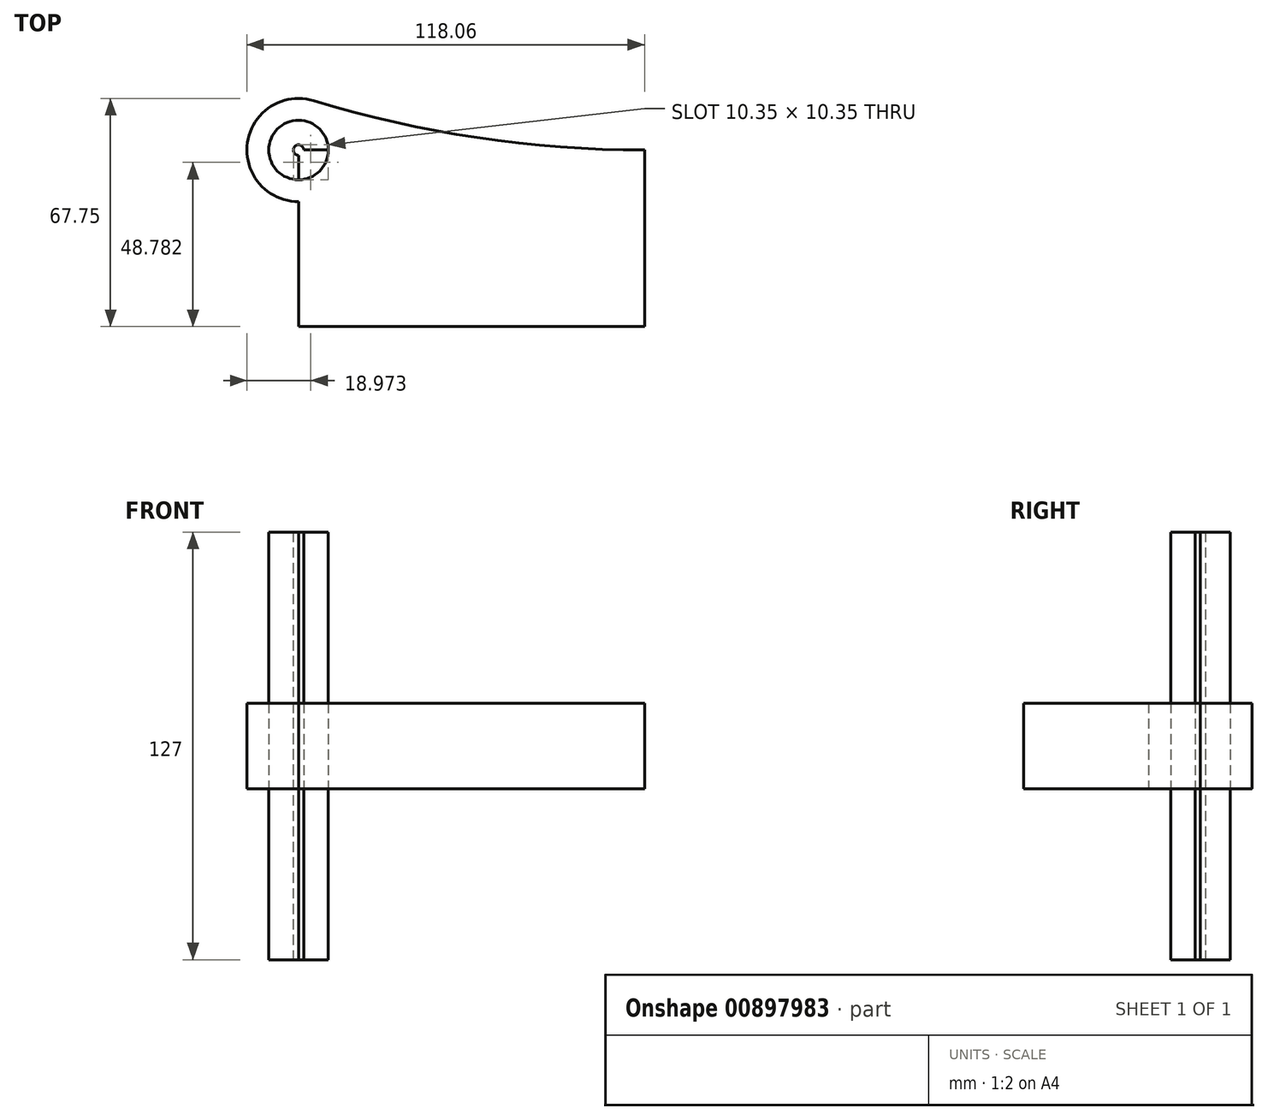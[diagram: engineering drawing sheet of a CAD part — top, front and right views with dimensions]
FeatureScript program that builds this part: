
annotation { "Feature Type Name" : "Feature", "Feature Type Description" : "" }
export const myFeature = defineFeature(function(context is Context, id is Id, definition is map)
    precondition{}
    {
        {
            var Q0;
            Q0=qCreatedBy(makeId("Top.planeOp"),FACE);
            var sketch = newSketch(context, id + "F0", { "sketchPlane" : qUnion([Q0])});
            skLineSegment(sketch, "E0.bottom", {"start": v(51.37, -26.22) * mm, "end": v(-51.37, -26.22) * mm});
            skLineSegment(sketch, "E0.top", {"start": v(51.37, 26.22) * mm, "end": v(-51.37, 26.22) * mm});
            skLineSegment(sketch, "E0.left", {"start": v(51.37, -26.22) * mm, "end": v(51.37, 26.22) * mm});
            skLineSegment(sketch, "E0.right", {"start": v(-51.37, -26.22) * mm, "end": v(-51.37, 26.22) * mm});
            skPoint(sketch, "E0.middle", {"position": v(0, 0) * mm});
            skCircle(sketch, "E1", {"center": v(-51.37, 26.22) * mm, "radius": 15.32 * mm});
            skArc(sketch, "E2", {"start": v(-46.9, 40.87) * mm, "mid": v(1.7, 29.9) * mm, "end": v(51.37, 26.22) * mm});
            skCircle(sketch, "E3", {"center": v(-51.37, 26.22) * mm, "radius": 1.55 * mm});
            skCircle(sketch, "E4", {"center": v(-51.37, 26.22) * mm, "radius": 8.83 * mm});
            skSolve(sketch);
        }
        {
            var Q0;
            {var subQ0=sQuery(id+"F0.wireOp",EDGE,"E4");var subQ1=sQuery(id+"F0.wireOp",EDGE,"E0.top");var subQ2=makeQuery(id+"F0.imprint","INTERSECT",VERTEX,{"derivedFrom":[subQ1,subQ0]});Q0=makeQuery(id+"F0.imprint","IMPRINT",FACE,{"disambiguationData":[TD([[makeQuery(id+"F0.imprint","IMPRINT",EDGE,{"disambiguationData":[TD([[subQ2,-1.0]])],"derivedFrom":subQ1}),-1.0]])]});}
            var Q1;
            {var subQ0=sQuery(id+"F0.wireOp",EDGE,"E1");var subQ1=sQuery(id+"F0.wireOp",EDGE,"E0.top");var subQ2=makeQuery(id+"F0.imprint","INTERSECT",VERTEX,{"derivedFrom":[subQ1,subQ0]});Q1=makeQuery(id+"F0.imprint","IMPRINT",FACE,{"disambiguationData":[TD([[makeQuery(id+"F0.imprint","IMPRINT",EDGE,{"disambiguationData":[TD([[subQ2,-1.0]])],"derivedFrom":subQ1}),1.0]])]});}
            var Q2;
            {var subQ0=sQuery(id+"F0.wireOp",EDGE,"E2");Q2=makeQuery(id+"F0.imprint","IMPRINT",FACE,{"disambiguationData":[TD([[makeQuery(id+"F0.imprint","IMPRINT",EDGE,{"derivedFrom":subQ0}),-1.0]])]});}
            var Q3;
            {var subQ0=sQuery(id+"F0.wireOp",EDGE,"E1");var subQ4=sQuery(id+"F0.wireOp",EDGE,"E0.top");var subQ5=makeQuery(id+"F0.imprint","INTERSECT",VERTEX,{"derivedFrom":[subQ4,subQ0]});Q3=makeQuery(id+"F0.imprint","IMPRINT",FACE,{"disambiguationData":[TD([[makeQuery(id+"F0.imprint","IMPRINT",EDGE,{"disambiguationData":[TD([[subQ5,-1.0]])],"derivedFrom":subQ4}),-1.0]])]});}
            var Q4;
            {var subQ1=sQuery(id+"F0.wireOp",EDGE,"E0.bottom");Q4=makeQuery(id+"F0.imprint","IMPRINT",FACE,{"disambiguationData":[TD([[makeQuery(id+"F0.imprint","IMPRINT",EDGE,{"derivedFrom":subQ1}),-1.0]])]});}
            extrude(context, id + "F1", {"entities" : qUnion([Q0, Q1, Q2, Q3, Q4]), "endBound" : BoundingType.SYMMETRIC, "depth" : 25.4 * mm, "offsetDistance" : 25.4 * mm});
        }
        {
            var Q0;
            {var subQ0=sQuery(id+"F0.wireOp",EDGE,"E4");var subQ1=sQuery(id+"F0.wireOp",EDGE,"E0.top");var subQ2=makeQuery(id+"F0.imprint","INTERSECT",VERTEX,{"derivedFrom":[subQ1,subQ0]});Q0=makeQuery(id+"F0.imprint","IMPRINT",FACE,{"disambiguationData":[TD([[makeQuery(id+"F0.imprint","IMPRINT",EDGE,{"disambiguationData":[TD([[subQ2,-1.0]])],"derivedFrom":subQ1}),-1.0]])]});}
            extrude(context, id + "F2", {"entities" : qUnion([Q0]), "endBound" : BoundingType.SYMMETRIC, "depth" : 127 * mm, "offsetDistance" : 25.4 * mm});
        }
    });
